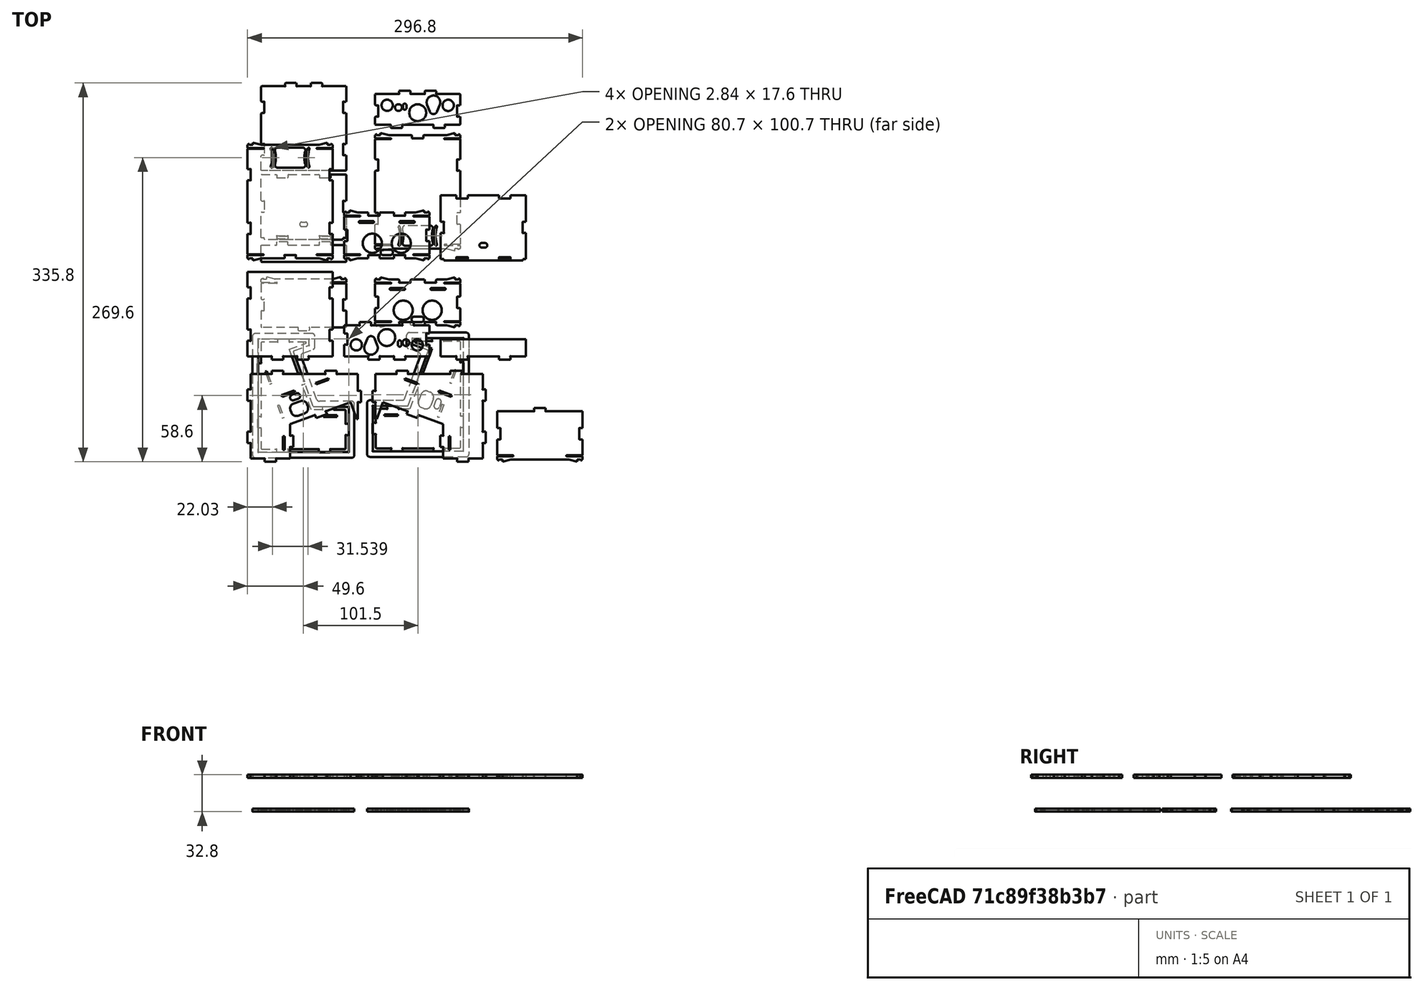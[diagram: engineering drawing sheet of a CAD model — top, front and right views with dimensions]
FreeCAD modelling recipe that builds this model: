
FCSTD DOCUMENT  (FreeCAD 1.0R39285 (Git))
Label: TheThing_v8_tabs_export
License: CERN Open Hardware Licence permissive
LicenseURL: https://cern-ohl.web.cern.ch/
objects: Part::Part2DObjectPython×13, Part::Feature×11, App::FeaturePython×11, Part::Chamfer×9, Sketcher::SketchObject×3, App::DocumentObjectGroup×1
note: 39 computed .brp shape members not serialized (recipe doc carries the construction recipe); baked Part::Feature solids carry a one-line shape summary decoded from their .brp

FEATURE [Part::Feature] test
  Placement = pos=(37.4,60.5,67.8) rot=(0,1,0;1.5708rad)
  shape: bbox 100.6 x 80.6 x 2.8 mm, 82 faces (baked)
FEATURE [Part::Feature] test001
  Placement = pos=(173.8,60.5,67.8) rot=(0,-1,0;1.5708rad)
  shape: bbox 100.6 x 80.6 x 2.8 mm, 70 faces (baked)
FEATURE [Part::Feature] test002
  Placement = pos=(259,27.5,93.2) rot=(0,-1,0;3.14159rad)
  shape: bbox 75.6 x 47.6 x 2.8 mm, 50 faces (baked)
FEATURE [Part::Feature] test003
  Placement = pos=(37.8,151.1,67.4) rot=(0,0,1;0rad)
  shape: bbox 75.6 x 77.8 x 2.8 mm, 42 faces (baked)
FEATURE [Part::Feature] test004
  Placement = pos=(123.4,151.1,33.2) rot=(0,-1,0;3.14159rad)
  shape: bbox 75.6 x 33.14 x 2.8 mm, 54 faces (baked)
FEATURE [Part::Feature] test005
  Placement = pos=(209,64.9222,78.0359) rot=(-0.34202,0,0;2.79253rad)
  shape: bbox 75.6 x 17.92 x 2.8 mm, 18 faces (baked)
FEATURE [Part::Feature] test006
  Placement = pos=(37.8,243.6,12.7) rot=(1,0,0;1.5708rad)
  shape: bbox 75.6 x 104.6 x 2.8 mm, 104 faces (baked)
FEATURE [Part::Feature] test007
  Placement = pos=(123.4,217.8,-27.7) rot=(-1,0,0;1.5708rad)
  shape: bbox 75.6 x 44.6 x 2.8 mm, 108 faces (baked)
FEATURE [Part::Feature] test008
  Placement = pos=(209,188.16,4.32219) rot=(-0.939693,0,0;1.22173rad)
  shape: bbox 75.6 x 58.11 x 2.925 mm, 56 faces (baked)
FEATURE [Part::Feature] test009
  Placement = pos=(171.3,46.5,-33) rot=(0.57735,0.57735,0.57735;4.18879rad)
  shape: bbox 90.2 x 110.2 x 2.8 mm, 46 faces (baked)
FEATURE [Part::Feature] test010
  Placement = pos=(29.4,45.7,-33) rot=(0.57735,-0.57735,-0.57735;4.18879rad)
  shape: bbox 90.2 x 110.2 x 2.8 mm, 46 faces (baked)
FEATURE [Part::Chamfer] Chamfer
  Base = -> test
  EdgeLinks = -> test [Edge25,Edge27,Edge39,Edge50,Edge52,Edge72,Edge74,Edge86,Edge97,Edge99,Edge119,Edge121,Edge133,Edge144,Edge146,Edge158,Edge169,Edge171,Edge194,Edge196]
  Edges = 20 edges r=0.5: [Edge25,Edge27,Edge39,Edge50,Edge52,Edge72,Edge74,Edge86,Edge97,Edge99,Edge119,Edge121,Edge133,Edge144,Edge146,Edge158,Edge169,Edge171,Edge194,Edge196]
  Placement = pos=(110.8,9.1,32.8) rot=(0.707107,0.707107,0;3.14159rad)
FEATURE [Part::Chamfer] Chamfer001
  Base = -> test001
  EdgeLinks = -> test001 [Edge25,Edge27,Edge39,Edge50,Edge52,Edge72,Edge74,Edge86,Edge97,Edge99,Edge119,Edge121,Edge133,Edge144,Edge146,Edge158,Edge169,Edge171,Edge194,Edge196]
  Edges = 20 edges r=0.5: [Edge25,Edge27,Edge39,Edge50,Edge52,Edge72,Edge74,Edge86,Edge97,Edge99,Edge119,Edge121,Edge133,Edge144,Edge146,Edge158,Edge169,Edge171,Edge194,Edge196]
  Placement = pos=(89.8,219.5,32.8) rot=(-0.707107,0.707107,0;3.14159rad)
FEATURE [Part::Chamfer] Chamfer002
  Base = -> test002
  EdgeLinks = -> test002 [Edge4,Edge6,Edge17,Edge20,Edge87,Edge103,Edge106,Edge120]
  Edges = 8 edges r=0.5: [Edge4,Edge6,Edge17,Edge20,Edge87,Edge103,Edge106,Edge120]
  Placement = pos=(308.8,163.8,-30) rot=(0,0,1;3.14159rad)
FEATURE [Part::Chamfer] Chamfer003
  Base = -> test003
  EdgeLinks = -> test003 [Edge1,Edge2,Edge7,Edge9,Edge27,Edge30,Edge45,Edge48,Edge59,Edge61,Edge81,Edge83,Edge95,Edge98,Edge121,Edge122]
  Edges = 16 edges r=0.5: [Edge1,Edge2,Edge7,Edge9,Edge27,Edge30,Edge45,Edge48,Edge59,Edge61,Edge81,Edge83,Edge95,Edge98,Edge121,Edge122]
  Placement = pos=(87.6,426.4,-30) rot=(0,0,1;3.14159rad)
FEATURE [Part::Chamfer] Chamfer004
  Base = -> test004
  EdgeLinks = -> test004 [Edge4,Edge7,Edge17,Edge20,Edge39,Edge42,Edge52,Edge55,Edge69,Edge73,Edge85,Edge88,Edge107,Edge110,Edge115,Edge123]
  Edges = 16 edges r=0.5: [Edge4,Edge7,Edge17,Edge20,Edge39,Edge42,Edge52,Edge55,Edge69,Edge73,Edge85,Edge88,Edge107,Edge110,Edge115,Edge123]
  Placement = pos=(274.2,419.6,-30) rot=(0,0,1;3.14159rad)
FEATURE [Part::Chamfer] Chamfer005
  Base = -> test005
  EdgeLinks = -> test005 [Edge1,Edge2,Edge5,Edge8,Edge28,Edge31,Edge50,Edge53]
  Edges = 8 edges r=0.5: [Edge1,Edge2,Edge5,Edge8,Edge28,Edge31,Edge50,Edge53]
  Placement = pos=(258.8,285.6,-30) rot=(0,0,1;3.14159rad)
FEATURE [Part::Chamfer] Chamfer006
  Base = -> test006
  EdgeLinks = -> test006 [Edge227,Edge232,Edge233,Edge238,Edge267,Edge272,Edge273,Edge278,Edge293,Edge298]
  Edges = 10 edges r=0.5: [Edge227,Edge232,Edge233,Edge238,Edge267,Edge272,Edge273,Edge278,Edge293,Edge298]
  Placement = pos=(188.6,470,-30) rot=(0,0,1;3.14159rad)
FEATURE [Part::Chamfer] Chamfer007
  Base = -> test007
  EdgeLinks = -> test007 [Edge243,Edge248,Edge249,Edge254,Edge269,Edge274,Edge289,Edge294,Edge295,Edge300,Edge315,Edge320]
  Edges = 12 edges r=0.5: [Edge243,Edge248,Edge249,Edge254,Edge269,Edge274,Edge289,Edge294,Edge295,Edge300,Edge315,Edge320]
  Placement = pos=(27.4,-59.4,-30) rot=(0,0,1;0rad)
FEATURE [Part::Chamfer] Chamfer008
  Base = -> test008
  EdgeLinks = -> test008 [Edge2,Edge4,Edge104,Edge105,Edge107,Edge118,Edge142,Edge143,Edge148,Edge149,Edge150,Edge155,Edge156,Edge164]
  Edges = 14 edges r=0.5: [Edge2,Edge4,Edge104,Edge105,Edge107,Edge118,Edge142,Edge143,Edge148,Edge149,Edge150,Edge155,Edge156,Edge164]
  Placement = pos=(-159.2,18.6,-30) rot=(0,0,1;0rad)
FEATURE [Sketcher::SketchObject] Sketch
  ArcFitTolerance = 1e-06
  FullyConstrained = true
  MakeInternals = false
  sketch-geometry (52):
    g0: LineSegment StartX=5 StartY=0 StartZ=0 EndX=95 EndY=0 EndZ=0
    g1: LineSegment StartX=100 StartY=5 StartZ=0 EndX=100 EndY=165 EndZ=0
    g2: LineSegment StartX=95 StartY=170 StartZ=0 EndX=5 EndY=170 EndZ=0
    g3: LineSegment StartX=0 StartY=165 StartZ=0 EndX=0 EndY=5 EndZ=0
    g4: LineSegment StartX=5 StartY=171 StartZ=0 EndX=95 EndY=171 EndZ=0
    g5: LineSegment StartX=100 StartY=176 StartZ=0 EndX=100 EndY=336 EndZ=0
    g6: LineSegment StartX=95 StartY=341 StartZ=0 EndX=5 EndY=341 EndZ=0
    g7: LineSegment StartX=0 StartY=336 StartZ=0 EndX=0 EndY=176 EndZ=0
    g8: LineSegment StartX=106 StartY=171 StartZ=0 EndX=196 EndY=171 EndZ=0
    g9: LineSegment StartX=201 StartY=176 StartZ=0 EndX=201 EndY=336 EndZ=0
    g10: LineSegment StartX=196 StartY=341 StartZ=0 EndX=106 EndY=341 EndZ=0
    g11: LineSegment StartX=101 StartY=336 StartZ=0 EndX=101 EndY=176 EndZ=0
    g12: LineSegment StartX=106 StartY=0 StartZ=0 EndX=196 EndY=0 EndZ=0
    g13: LineSegment StartX=201 StartY=5 StartZ=0 EndX=201 EndY=165 EndZ=0
    g14: LineSegment StartX=196 StartY=170 StartZ=0 EndX=106 EndY=170 EndZ=0
    g15: LineSegment StartX=101 StartY=165 StartZ=0 EndX=101 EndY=5 EndZ=0
    g16: LineSegment [constr] StartX=100 StartY=170 StartZ=0 EndX=101 EndY=170 EndZ=0
    g17: LineSegment [constr] StartX=101 StartY=170 StartZ=0 EndX=101 EndY=171 EndZ=0
    g18: LineSegment [constr] StartX=101 StartY=171 StartZ=0 EndX=100 EndY=171 EndZ=0
    g19: LineSegment [constr] StartX=100 StartY=171 StartZ=0 EndX=100 EndY=170 EndZ=0
    g20: ArcOfCircle CenterX=5 CenterY=5 CenterZ=0 NormalX=0 NormalY=0 NormalZ=1 AngleXU=0 Radius=5 StartAngle=3.14159 EndAngle=4.71239
    g21: GeomPoint [constr] X=0 Y=0 Z=0
    g22: ArcOfCircle CenterX=95 CenterY=5 CenterZ=0 NormalX=0 NormalY=0 NormalZ=1 AngleXU=0 Radius=5 StartAngle=4.71239 EndAngle=6.28319
    g23: GeomPoint [constr] X=100 Y=0 Z=0
    g24: ArcOfCircle CenterX=106 CenterY=5 CenterZ=0 NormalX=0 NormalY=0 NormalZ=1 AngleXU=0 Radius=5 StartAngle=3.14159 EndAngle=4.71239
    g25: GeomPoint [constr] X=101 Y=0 Z=0
    g26: ArcOfCircle CenterX=196 CenterY=5 CenterZ=0 NormalX=0 NormalY=0 NormalZ=1 AngleXU=0 Radius=5 StartAngle=4.71239 EndAngle=6.28319
    g27: GeomPoint [constr] X=201 Y=0 Z=0
    g28: ArcOfCircle CenterX=95 CenterY=176 CenterZ=0 NormalX=0 NormalY=0 NormalZ=1 AngleXU=0 Radius=5 StartAngle=4.71239 EndAngle=6.28319
    g29: GeomPoint [constr] X=100 Y=171 Z=0
    g30: ArcOfCircle CenterX=95 CenterY=165 CenterZ=0 NormalX=0 NormalY=0 NormalZ=1 AngleXU=0 Radius=5 StartAngle=3e-16 EndAngle=1.5708
    g31: GeomPoint [constr] X=100 Y=170 Z=0
    g32: ArcOfCircle CenterX=106 CenterY=165 CenterZ=0 NormalX=0 NormalY=0 NormalZ=1 AngleXU=0 Radius=5 StartAngle=1.5708 EndAngle=3.14159
    g33: GeomPoint [constr] X=101 Y=170 Z=0
    g34: ArcOfCircle CenterX=106 CenterY=176 CenterZ=0 NormalX=0 NormalY=0 NormalZ=1 AngleXU=0 Radius=5 StartAngle=3.14159 EndAngle=4.71239
    g35: GeomPoint [constr] X=101 Y=171 Z=0
    g36: ArcOfCircle CenterX=5 CenterY=176 CenterZ=0 NormalX=0 NormalY=0 NormalZ=1 AngleXU=0 Radius=5 StartAngle=3.14159 EndAngle=4.71239
    g37: GeomPoint [constr] X=0 Y=171 Z=0
    g38: ArcOfCircle CenterX=196 CenterY=176 CenterZ=0 NormalX=0 NormalY=0 NormalZ=1 AngleXU=0 Radius=5 StartAngle=4.71239 EndAngle=6.28319
    g39: GeomPoint [constr] X=201 Y=171 Z=0
    g40: ArcOfCircle CenterX=196 CenterY=165 CenterZ=0 NormalX=0 NormalY=0 NormalZ=1 AngleXU=0 Radius=5 StartAngle=2.4e-15 EndAngle=1.5708
    g41: GeomPoint [constr] X=201 Y=170 Z=0
    g42: ArcOfCircle CenterX=5 CenterY=165 CenterZ=0 NormalX=0 NormalY=0 NormalZ=1 AngleXU=0 Radius=5 StartAngle=1.5708 EndAngle=3.14159
    g43: GeomPoint [constr] X=0 Y=170 Z=0
    g44: ArcOfCircle CenterX=5 CenterY=336 CenterZ=0 NormalX=0 NormalY=0 NormalZ=1 AngleXU=0 Radius=5 StartAngle=1.5708 EndAngle=3.14159
    g45: GeomPoint [constr] X=0 Y=341 Z=0
    g46: ArcOfCircle CenterX=95 CenterY=336 CenterZ=0 NormalX=0 NormalY=0 NormalZ=1 AngleXU=0 Radius=5 StartAngle=1.7e-15 EndAngle=1.5708
    g47: GeomPoint [constr] X=100 Y=341 Z=0
    g48: ArcOfCircle CenterX=106 CenterY=336 CenterZ=0 NormalX=0 NormalY=0 NormalZ=1 AngleXU=0 Radius=5 StartAngle=1.5708 EndAngle=3.14159
    g49: GeomPoint [constr] X=101 Y=341 Z=0
    g50: ArcOfCircle CenterX=196 CenterY=336 CenterZ=0 NormalX=0 NormalY=0 NormalZ=1 AngleXU=0 Radius=5 StartAngle=-2.7e-15 EndAngle=1.5708
    g51: GeomPoint [constr] X=201 Y=341 Z=0
  constraints (119):
    c: Horizontal(g0)
    c: Horizontal(g2)
    c: Vertical(g1)
    c: Vertical(g3)
    c: Coincident(g21,g-1)
    c: Horizontal(g4)
    c: Horizontal(g6)
    c: Vertical(g5)
    c: Vertical(g7)
    c: Horizontal(g8)
    c: Horizontal(g10)
    c: Vertical(g9)
    c: Vertical(g11)
    c: Horizontal(g12)
    c: Horizontal(g14)
    c: Vertical(g13)
    c: Vertical(g15)
    c: DistanceX(g21,g23) = 100
    c: DistanceY(g21,g43) = 170
    c: Coincident(g16,g17)
    c: Coincident(g17,g18)
    c: Coincident(g18,g19)
    c: Coincident(g19,g16)
    c: Horizontal(g16)
    c: Horizontal(g18)
    c: Vertical(g17)
    c: Vertical(g19)
    c: Distance(g17,g19) = 1
    c: Distance(g16,g18) = 1
    c: Coincident(g16,g31)
    c: Coincident(g18,g29)
    c: Coincident(g17,g35)
    c: Coincident(g16,g33)
    c: PointOnObject(g21,g0)
    c: PointOnObject(g21,g3)
    c: Tangent(g0,g20) = -1.5708
    c: Tangent(g3,g20) = -1.5708
    c: PointOnObject(g23,g0)
    c: PointOnObject(g23,g1)
    c: Tangent(g0,g22) = -1.5708
    c: Tangent(g1,g22) = -1.5708
    c: PointOnObject(g25,g12)
    c: PointOnObject(g25,g15)
    c: Tangent(g12,g24) = -1.5708
    c: Tangent(g15,g24) = -1.5708
    c: PointOnObject(g27,g13)
    c: PointOnObject(g27,g12)
    c: Tangent(g13,g26) = -1.5708
    c: Tangent(g12,g26) = -1.5708
    c: PointOnObject(g29,g5)
    c: PointOnObject(g29,g4)
    c: Tangent(g5,g28) = -1.5708
    c: Tangent(g4,g28) = -1.5708
    c: PointOnObject(g31,g2)
    c: PointOnObject(g31,g1)
    c: Tangent(g2,g30) = -1.5708
    c: Tangent(g1,g30) = -1.5708
    c: PointOnObject(g33,g14)
    c: PointOnObject(g33,g15)
    c: Tangent(g14,g32) = -1.5708
    c: Tangent(g15,g32) = -1.5708
    c: PointOnObject(g35,g8)
    c: PointOnObject(g35,g11)
    c: Tangent(g8,g34) = -1.5708
    c: Tangent(g11,g34) = -1.5708
    c: PointOnObject(g37,g4)
    c: PointOnObject(g37,g7)
    c: Tangent(g4,g36) = -1.5708
    c: Tangent(g7,g36) = -1.5708
    c: PointOnObject(g39,g8)
    c: PointOnObject(g39,g9)
    c: Tangent(g8,g38) = -1.5708
    c: Tangent(g9,g38) = -1.5708
    c: PointOnObject(g41,g14)
    c: PointOnObject(g41,g13)
    c: Tangent(g14,g40) = -1.5708
    c: Tangent(g13,g40) = -1.5708
    c: PointOnObject(g43,g2)
    c: PointOnObject(g43,g3)
    c: Tangent(g2,g42) = -1.5708
    c: Tangent(g3,g42) = -1.5708
    c: PointOnObject(g45,g6)
    c: PointOnObject(g45,g7)
    c: Tangent(g6,g44) = -1.5708
    c: Tangent(g7,g44) = -1.5708
    c: PointOnObject(g47,g6)
    c: PointOnObject(g47,g5)
    c: Tangent(g6,g46) = -1.5708
    c: Tangent(g5,g46) = -1.5708
    c: PointOnObject(g49,g10)
    c: PointOnObject(g49,g11)
    c: Tangent(g10,g48) = -1.5708
    c: Tangent(g11,g48) = -1.5708
    c: PointOnObject(g51,g10)
    c: PointOnObject(g51,g9)
    c: Tangent(g10,g50) = -1.5708
    c: Tangent(g9,g50) = -1.5708
    c: Equal(g50,g48)
    c: Equal(g48,g46)
    c: Equal(g46,g44)
    c: Equal(g44,g36)
    c: Equal(g36,g42)
    c: Equal(g42,g28)
    c: Equal(g28,g34)
    c: Equal(g34,g32)
    c: Equal(g32,g30)
    c: Equal(g30,g38)
    c: Equal(g38,g40)
    c: Equal(g40,g26)
    c: Equal(g26,g24)
    c: Equal(g24,g22)
    c: Equal(g22,g20)
    c: Radius(g20) = 5
    c: Vertical(g37,g43)
    c: Horizontal(g25,g23)
    c: Vertical(g39,g41)
    c: Horizontal(g47,g49)
    c: Equal(g7,g3)
    c: Equal(g6,g10)
FEATURE [Part::Part2DObjectPython] Shape2DView  # Draft 2D object (typed FeaturePython)
  AutoUpdate = true
  Clip = false
  FuseArch = false
  HiddenLines = false
  InPlace = true
  OnlySolids = false
  Placement = pos=(96,354,3) rot=(0,0,1;1.5708rad)
  Projection = (-0.0061258,0.0189136,0.999802)
  ProjectionMode = 0
  SegmentLength = 0.05
  Tessellation = false
  VisibleOnly = false
FEATURE [Part::Part2DObjectPython] Shape2DView001  # Draft 2D object (typed FeaturePython)
  AutoUpdate = true
  Clip = false
  FuseArch = false
  HiddenLines = false
  InPlace = true
  OnlySolids = false
  Placement = pos=(138,7,3) rot=(0,0,1;3.14159rad)
  Projection = (0,0,1)
  ProjectionMode = 0
  SegmentLength = 0.05
  Tessellation = false
  VisibleOnly = false
FEATURE [App::FeaturePython] Text  # WARN: FeaturePython — macro-defined, semantics opaque (R4)
  Placement = pos=(166,103,0) rot=(0,0,1;0rad)
  Text = [1]
FEATURE [App::FeaturePython] Text001  # WARN: FeaturePython — macro-defined, semantics opaque (R4)
  Placement = pos=(30,103,0) rot=(0,0,1;0rad)
  Text = [2]
FEATURE [App::FeaturePython] Text002  # WARN: FeaturePython — macro-defined, semantics opaque (R4)
  Placement = pos=(149,283,0) rot=(0,0,1;0rad)
  Text = [3]
FEATURE [App::FeaturePython] Text003  # WARN: FeaturePython — macro-defined, semantics opaque (R4)
  Placement = pos=(47,248,0) rot=(0,0,1;0rad)
  Text = [4]
FEATURE [App::FeaturePython] Text004  # WARN: FeaturePython — macro-defined, semantics opaque (R4)
  Placement = pos=(149,322,0) rot=(0,0,1;0rad)
  Text = [5]
FEATURE [App::FeaturePython] Text005  # WARN: FeaturePython — macro-defined, semantics opaque (R4)
  Placement = pos=(150,155,0) rot=(0,0,1;0rad)
  Text = [6]
FEATURE [App::FeaturePython] Text006  # WARN: FeaturePython — macro-defined, semantics opaque (R4)
  Placement = pos=(47,329,0) rot=(0,0,1;0rad)
  Text = [7]
FEATURE [App::FeaturePython] Text007  # WARN: FeaturePython — macro-defined, semantics opaque (R4)
  Placement = pos=(47,158,0) rot=(0,0,1;0rad)
  Text = [8]
FEATURE [App::FeaturePython] Text008  # WARN: FeaturePython — macro-defined, semantics opaque (R4)
  Placement = pos=(47,189,0) rot=(0,0,1;0rad)
  Text = [9]
FEATURE [App::FeaturePython] Text009  # WARN: FeaturePython — macro-defined, semantics opaque (R4)
  Placement = pos=(165,111,0) rot=(0,0,1;0rad)
  Text = [10]
FEATURE [App::FeaturePython] Text010  # WARN: FeaturePython — macro-defined, semantics opaque (R4)
  Placement = pos=(29,110,0) rot=(0,0,1;0rad)
  Text = [11]
FEATURE [Part::Part2DObjectPython] Shape2DView002  # Draft 2D object (typed FeaturePython)
  AutoUpdate = true
  Base = -> Chamfer008
  Clip = false
  FuseArch = false
  HiddenLines = false
  InPlace = true
  OnlySolids = false
  Projection = (0,0,1)
  ProjectionMode = 0
  SegmentLength = 0.05
  Tessellation = false
  VisibleOnly = false
FEATURE [Sketcher::SketchObject] Sketch001
  ArcFitTolerance = 1e-06
  FullyConstrained = false
  MakeInternals = false
  sketch-geometry (76):
    g0: LineSegment StartX=12.5 StartY=254.796 StartZ=0 EndX=25.425 EndY=254.796 EndZ=0
    g1: LineSegment StartX=14.8 StartY=198.4 StartZ=0 EndX=12.5 EndY=198.4 EndZ=0
    g2: LineSegment StartX=12.5 StartY=198.4 StartZ=0 EndX=12 EndY=198.9 EndZ=0
    g3: LineSegment StartX=14.8 StartY=197.5 StartZ=0 EndX=14.8 EndY=198.4 EndZ=0
    g4: LineSegment StartX=12 StartY=198.9 StartZ=0 EndX=12 EndY=220.843 EndZ=0
    g5: LineSegment StartX=14.8 StartY=197.5 StartZ=0 EndX=15.3 EndY=197 EndZ=0
    g6: LineSegment StartX=12.5 StartY=221.343 StartZ=0 EndX=12 EndY=220.843 EndZ=0
    g7: LineSegment StartX=25.8826 StartY=197 StartZ=0 EndX=15.3 EndY=197 EndZ=0
    g8: LineSegment StartX=12.5 StartY=221.343 StartZ=0 EndX=14.5913 EndY=221.343 EndZ=0
    g9: ArcOfEllipse CenterX=26.0227 CenterY=196.855 CenterZ=0 NormalX=0 NormalY=0 NormalZ=1 MajorRadius=0.207869 MinorRadius=0.195333 AngleXU=1.5708 StartAngle=0.523599 EndAngle=0.799258
    g10: ArcOfCircle CenterX=14.7648 CenterY=221.443 CenterZ=0 NormalX=0 NormalY=0 NormalZ=1 AngleXU=0 Radius=0.200333 StartAngle=3.66519 EndAngle=6.28319
    g11: LineSegment StartX=25.925 StartY=199.585 StartZ=0 EndX=25.925 EndY=197.035 EndZ=0
    g12: ArcOfCircle CenterX=14.7648 CenterY=221.443 CenterZ=0 NormalX=0 NormalY=0 NormalZ=1 AngleXU=0 Radius=0.200333 StartAngle=0 EndAngle=1.0472
    g13: ArcOfEllipse CenterX=26.0227 CenterY=199.765 CenterZ=0 NormalX=0 NormalY=0 NormalZ=1 MajorRadius=0.207869 MinorRadius=0.195333 AngleXU=1.5708 StartAngle=1.5708 EndAngle=2.61799
    g14: ArcOfEllipse CenterX=26.0227 CenterY=199.765 CenterZ=0 NormalX=0 NormalY=0 NormalZ=1 MajorRadius=0.207869 MinorRadius=0.195333 AngleXU=1.5708 StartAngle=5.23599 EndAngle=7.85398
    g15: LineSegment StartX=14.865 StartY=231.019 StartZ=0 EndX=14.865 EndY=221.616 EndZ=0
    g16: LineSegment StartX=35.6082 StartY=199.869 StartZ=0 EndX=26.1918 EndY=199.869 EndZ=0
    g17: ArcOfCircle CenterX=14.7648 CenterY=231.192 CenterZ=0 NormalX=0 NormalY=0 NormalZ=1 AngleXU=0 Radius=0.200333 StartAngle=5.23599 EndAngle=6.28319
    g18: ArcOfEllipse CenterX=35.7773 CenterY=199.765 CenterZ=0 NormalX=0 NormalY=0 NormalZ=1 MajorRadius=0.207869 MinorRadius=0.195333 AngleXU=1.5708 StartAngle=4.71239 EndAngle=7.33038
    g19: ArcOfEllipse CenterX=35.7773 CenterY=199.765 CenterZ=0 NormalX=0 NormalY=0 NormalZ=1 MajorRadius=0.207869 MinorRadius=0.195333 AngleXU=1.5708 StartAngle=3.66519 EndAngle=4.71239
    g20: ArcOfCircle CenterX=14.7648 CenterY=231.192 CenterZ=0 NormalX=0 NormalY=0 NormalZ=1 AngleXU=0 Radius=0.200333 StartAngle=0 EndAngle=2.61799
    g21: LineSegment StartX=35.875 StartY=199.585 StartZ=0 EndX=35.875 EndY=197.035 EndZ=0
    g22: LineSegment StartX=12.5 StartY=231.293 StartZ=0 EndX=14.5913 EndY=231.293 EndZ=0
    g23: ArcOfEllipse CenterX=35.7773 CenterY=196.855 CenterZ=0 NormalX=0 NormalY=0 NormalZ=1 MajorRadius=0.207869 MinorRadius=0.195333 AngleXU=1.5708 StartAngle=5.48393 EndAngle=5.75959
    g24: LineSegment StartX=12 StartY=231.793 StartZ=0 EndX=12.5 EndY=231.293 EndZ=0
    g25: LineSegment StartX=63.6826 StartY=197 StartZ=0 EndX=35.9174 EndY=197 EndZ=0
    g26: LineSegment StartX=12 StartY=231.793 StartZ=0 EndX=12 EndY=254.296 EndZ=0
    g27: ArcOfEllipse CenterX=63.8227 CenterY=196.855 CenterZ=0 NormalX=0 NormalY=0 NormalZ=1 MajorRadius=0.207869 MinorRadius=0.195333 AngleXU=1.5708 StartAngle=0.523599 EndAngle=0.799258
    g28: LineSegment StartX=12.5 StartY=254.796 StartZ=0 EndX=12 EndY=254.296 EndZ=0
    g29: LineSegment StartX=63.725 StartY=199.585 StartZ=0 EndX=63.725 EndY=197.035 EndZ=0
    g30: ArcOfEllipse CenterX=63.8227 CenterY=199.765 CenterZ=0 NormalX=0 NormalY=0 NormalZ=1 MajorRadius=0.207869 MinorRadius=0.195333 AngleXU=1.5708 StartAngle=1.5708 EndAngle=2.61799
    g31: ArcOfEllipse CenterX=63.8227 CenterY=199.765 CenterZ=0 NormalX=0 NormalY=0 NormalZ=1 MajorRadius=0.207869 MinorRadius=0.195333 AngleXU=1.5708 StartAngle=5.23599 EndAngle=7.85398
    g32: LineSegment StartX=25.425 StartY=254.796 StartZ=0 EndX=25.925 EndY=254.296 EndZ=0
    g33: LineSegment StartX=73.4082 StartY=199.869 StartZ=0 EndX=63.9918 EndY=199.869 EndZ=0
    g34: LineSegment StartX=25.925 StartY=254.296 StartZ=0 EndX=25.925 EndY=252.204 EndZ=0
    g35: ArcOfEllipse CenterX=73.5773 CenterY=199.765 CenterZ=0 NormalX=0 NormalY=0 NormalZ=1 MajorRadius=0.207869 MinorRadius=0.195333 AngleXU=1.5708 StartAngle=4.71239 EndAngle=7.33038
    g36: ArcOfEllipse CenterX=73.5773 CenterY=199.765 CenterZ=0 NormalX=0 NormalY=0 NormalZ=1 MajorRadius=0.207869 MinorRadius=0.195333 AngleXU=1.5708 StartAngle=3.66519 EndAngle=4.71239
    g37: ArcOfCircle CenterX=26.0252 CenterY=252.031 CenterZ=0 NormalX=0 NormalY=0 NormalZ=1 AngleXU=-1.5708 Radius=0.200333 StartAngle=3.66519 EndAngle=6.28319
    g38: LineSegment StartX=73.675 StartY=199.585 StartZ=0 EndX=73.675 EndY=197.035 EndZ=0
    g39: ArcOfCircle CenterX=26.0252 CenterY=252.031 CenterZ=0 NormalX=0 NormalY=0 NormalZ=1 AngleXU=-1.5708 Radius=0.200333 StartAngle=0 EndAngle=1.0472
    g40: ArcOfEllipse CenterX=73.5773 CenterY=196.855 CenterZ=0 NormalX=0 NormalY=0 NormalZ=1 MajorRadius=0.207869 MinorRadius=0.195333 AngleXU=1.5708 StartAngle=5.48393 EndAngle=5.75959
    g41: LineSegment StartX=26.1987 StartY=251.931 StartZ=0 EndX=35.6013 EndY=251.931 EndZ=0
    g42: LineSegment StartX=84.3 StartY=197 StartZ=0 EndX=73.7174 EndY=197 EndZ=0
    g43: ArcOfCircle CenterX=35.7748 CenterY=252.031 CenterZ=0 NormalX=0 NormalY=0 NormalZ=1 AngleXU=-1.5708 Radius=0.200333 StartAngle=5.23599 EndAngle=6.28319
    g44: LineSegment StartX=84.3 StartY=197 StartZ=0 EndX=84.8 EndY=197.5 EndZ=0
    g45: ArcOfCircle CenterX=35.7748 CenterY=252.031 CenterZ=0 NormalX=0 NormalY=0 NormalZ=1 AngleXU=-1.5708 Radius=0.200333 StartAngle=0 EndAngle=2.61799
    g46: LineSegment StartX=84.8 StartY=198.4 StartZ=0 EndX=84.8 EndY=197.5 EndZ=0
    g47: LineSegment StartX=35.875 StartY=254.296 StartZ=0 EndX=35.875 EndY=252.204 EndZ=0
    g48: LineSegment StartX=87.1 StartY=198.4 StartZ=0 EndX=84.8 EndY=198.4 EndZ=0
    g49: LineSegment StartX=36.375 StartY=254.796 StartZ=0 EndX=35.875 EndY=254.296 EndZ=0
    g50: LineSegment StartX=87.1 StartY=198.4 StartZ=0 EndX=87.6 EndY=198.9 EndZ=0
    g51: LineSegment StartX=36.375 StartY=254.796 StartZ=0 EndX=63.225 EndY=254.796 EndZ=0
    g52: LineSegment StartX=87.6 StartY=220.843 StartZ=0 EndX=87.6 EndY=198.9 EndZ=0
    g53: LineSegment StartX=63.725 StartY=254.296 StartZ=0 EndX=63.225 EndY=254.796 EndZ=0
    g54: LineSegment StartX=87.6 StartY=220.843 StartZ=0 EndX=87.1 EndY=221.343 EndZ=0
    g55: LineSegment StartX=63.725 StartY=254.296 StartZ=0 EndX=63.725 EndY=252.204 EndZ=0
    g56: LineSegment StartX=85.0087 StartY=221.343 StartZ=0 EndX=87.1 EndY=221.343 EndZ=0
    g57: ArcOfCircle CenterX=63.8252 CenterY=252.031 CenterZ=0 NormalX=0 NormalY=0 NormalZ=1 AngleXU=-1.5708 Radius=0.200333 StartAngle=3.66519 EndAngle=6.28319
    g58: ArcOfCircle CenterX=84.8352 CenterY=221.443 CenterZ=0 NormalX=0 NormalY=0 NormalZ=1 AngleXU=0 Radius=0.200333 StartAngle=2.0944 EndAngle=5.75959
    g59: ArcOfCircle CenterX=63.8252 CenterY=252.031 CenterZ=0 NormalX=0 NormalY=0 NormalZ=1 AngleXU=-1.5708 Radius=0.200333 StartAngle=0 EndAngle=1.0472
    g60: LineSegment StartX=84.735 StartY=231.019 StartZ=0 EndX=84.735 EndY=221.616 EndZ=0
    g61: LineSegment StartX=63.9987 StartY=251.931 StartZ=0 EndX=73.4013 EndY=251.931 EndZ=0
    g62: ArcOfCircle CenterX=84.8352 CenterY=231.192 CenterZ=0 NormalX=0 NormalY=0 NormalZ=1 AngleXU=0 Radius=0.200333 StartAngle=0.523599 EndAngle=4.18879
    g63: ArcOfCircle CenterX=73.5748 CenterY=252.031 CenterZ=0 NormalX=0 NormalY=0 NormalZ=1 AngleXU=-1.5708 Radius=0.200333 StartAngle=5.23599 EndAngle=6.28319
    g64: LineSegment StartX=85.0087 StartY=231.293 StartZ=0 EndX=87.1 EndY=231.293 EndZ=0
    g65: ArcOfCircle CenterX=73.5748 CenterY=252.031 CenterZ=0 NormalX=0 NormalY=0 NormalZ=1 AngleXU=-1.5708 Radius=0.200333 StartAngle=0 EndAngle=2.61799
    g66: LineSegment StartX=87.1 StartY=231.293 StartZ=0 EndX=87.6 EndY=231.793 EndZ=0
    g67: LineSegment StartX=73.675 StartY=254.296 StartZ=0 EndX=73.675 EndY=252.204 EndZ=0
    g68: LineSegment StartX=87.6 StartY=254.296 StartZ=0 EndX=87.6 EndY=231.793 EndZ=0
    g69: LineSegment StartX=74.175 StartY=254.796 StartZ=0 EndX=73.675 EndY=254.296 EndZ=0
    g70: LineSegment StartX=87.6 StartY=254.296 StartZ=0 EndX=87.1 EndY=254.796 EndZ=0
    g71: LineSegment StartX=74.175 StartY=254.796 StartZ=0 EndX=87.1 EndY=254.796 EndZ=0
    g72: LineSegment StartX=48.3 StartY=212.512 StartZ=0 EndX=51.3 EndY=212.512 EndZ=0
    g73: ArcOfCircle CenterX=48.3 CenterY=210.512 CenterZ=0 NormalX=0 NormalY=0 NormalZ=1 AngleXU=0 Radius=2 StartAngle=1.5708 EndAngle=4.71239
    g74: ArcOfCircle CenterX=51.3 CenterY=210.512 CenterZ=0 NormalX=0 NormalY=0 NormalZ=1 AngleXU=0 Radius=2 StartAngle=4.71239 EndAngle=7.85398
    g75: LineSegment StartX=48.3 StartY=208.512 StartZ=0 EndX=51.3 EndY=208.512 EndZ=0
FEATURE [Part::Part2DObjectPython] Shape2DView003  # Draft 2D object (typed FeaturePython)
  AutoUpdate = true
  Base = -> test009
  Clip = false
  FuseArch = false
  HiddenLines = false
  InPlace = true
  OnlySolids = false
  Projection = (0,0,1)
  ProjectionMode = 0
  SegmentLength = 0.05
  Tessellation = false
  VisibleOnly = false
FEATURE [Part::Part2DObjectPython] Shape2DView004  # Draft 2D object (typed FeaturePython)
  AutoUpdate = true
  Base = -> test010
  Clip = false
  FuseArch = false
  HiddenLines = false
  InPlace = true
  OnlySolids = false
  Projection = (0,0,1)
  ProjectionMode = 0
  SegmentLength = 0.05
  Tessellation = false
  VisibleOnly = false
FEATURE [Part::Part2DObjectPython] Shape2DView005  # Draft 2D object (typed FeaturePython)
  AutoUpdate = true
  Base = -> Chamfer
  Clip = false
  FuseArch = false
  HiddenLines = false
  InPlace = true
  OnlySolids = false
  Projection = (0,0,1)
  ProjectionMode = 0
  SegmentLength = 0.05
  Tessellation = false
  VisibleOnly = false
FEATURE [Part::Part2DObjectPython] Shape2DView006  # Draft 2D object (typed FeaturePython)
  AutoUpdate = true
  Base = -> Chamfer001
  Clip = false
  FuseArch = false
  HiddenLines = false
  InPlace = true
  OnlySolids = false
  Projection = (0,0,1)
  ProjectionMode = 0
  SegmentLength = 0.05
  Tessellation = false
  VisibleOnly = false
FEATURE [Part::Part2DObjectPython] Shape2DView007  # Draft 2D object (typed FeaturePython)
  AutoUpdate = true
  Base = -> Chamfer002
  Clip = false
  FuseArch = false
  HiddenLines = false
  InPlace = true
  OnlySolids = false
  Projection = (0,0,1)
  ProjectionMode = 0
  SegmentLength = 0.05
  Tessellation = false
  VisibleOnly = false
FEATURE [Part::Part2DObjectPython] Shape2DView008  # Draft 2D object (typed FeaturePython)
  AutoUpdate = true
  Base = -> Chamfer003
  Clip = false
  FuseArch = false
  HiddenLines = false
  InPlace = true
  OnlySolids = false
  Projection = (0,0,1)
  ProjectionMode = 0
  SegmentLength = 0.05
  Tessellation = false
  VisibleOnly = false
FEATURE [Part::Part2DObjectPython] Shape2DView009  # Draft 2D object (typed FeaturePython)
  AutoUpdate = true
  Base = -> Chamfer004
  Clip = false
  FuseArch = false
  HiddenLines = false
  InPlace = true
  OnlySolids = false
  Projection = (0,0,1)
  ProjectionMode = 0
  SegmentLength = 0.05
  Tessellation = false
  VisibleOnly = false
FEATURE [Part::Part2DObjectPython] Shape2DView010  # Draft 2D object (typed FeaturePython)
  AutoUpdate = true
  Base = -> Chamfer005
  Clip = false
  FuseArch = false
  HiddenLines = false
  InPlace = true
  OnlySolids = false
  Projection = (0,0,1)
  ProjectionMode = 0
  SegmentLength = 0.05
  Tessellation = false
  VisibleOnly = false
FEATURE [Part::Part2DObjectPython] Shape2DView011  # Draft 2D object (typed FeaturePython)
  AutoUpdate = true
  Base = -> Chamfer006
  Clip = false
  FuseArch = false
  HiddenLines = false
  InPlace = true
  OnlySolids = false
  Projection = (0,0,1)
  ProjectionMode = 0
  SegmentLength = 0.05
  Tessellation = false
  VisibleOnly = false
FEATURE [Part::Part2DObjectPython] Shape2DView012  # Draft 2D object (typed FeaturePython)
  AutoUpdate = true
  Base = -> Chamfer007
  Clip = false
  FuseArch = false
  HiddenLines = false
  InPlace = true
  OnlySolids = false
  Projection = (0,0,1)
  ProjectionMode = 0
  SegmentLength = 0.05
  Tessellation = false
  VisibleOnly = false
FEATURE [App::DocumentObjectGroup] Group  label="Incoming_Solids"
  Group = -> [test009,test010,Chamfer,Chamfer001,Chamfer002,Chamfer003,Chamfer004,Chamfer005,Chamfer006,Chamfer007,Chamfer008,Shape2DView002]
FEATURE [Sketcher::SketchObject] Sketch002
  ArcFitTolerance = 1e-06
  ExternalGeometry = -> [Shape2DView008]
  FullyConstrained = true
  MakeInternals = false
  sketch-geometry (6):
    g0: LineSegment StartX=48.4 StartY=306 StartZ=0 EndX=48.4 EndY=296 EndZ=0
    g1: LineSegment StartX=48.4 StartY=296 StartZ=0 EndX=51.2 EndY=296 EndZ=0
    g2: LineSegment StartX=51.2 StartY=296 StartZ=0 EndX=51.2 EndY=306 EndZ=0
    g3: LineSegment StartX=51.2 StartY=306 StartZ=0 EndX=48.4 EndY=306 EndZ=0
    g4: GeomPoint [constr] X=49.8 Y=301 Z=0
    g5: LineSegment [constr] StartX=49.8 StartY=333 StartZ=0 EndX=49.8 EndY=306 EndZ=0
  constraints (15):
    c: Coincident(g0,g1)
    c: Coincident(g1,g2)
    c: Coincident(g2,g3)
    c: Coincident(g3,g0)
    c: Vertical(g0)
    c: Vertical(g2)
    c: Horizontal(g1)
    c: Horizontal(g3)
    c: Symmetric(g2,g0,g4)
    c: Distance(g1,g1) = 2.8
    c: DistanceY(g0,g0) = 10
    c: Symmetric(g-3,g-3,g5)
    c: Symmetric(g3,g3,g5)
    c: Vertical(g5)
    c: Distance(g0,g-4) = 38
